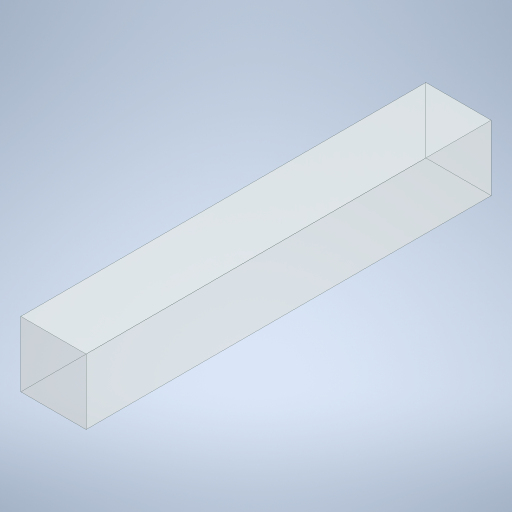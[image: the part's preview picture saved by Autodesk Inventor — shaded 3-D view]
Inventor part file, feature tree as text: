
AUTODESK INVENTOR PART (.ipt)
format: ipt  version: 2024 (Build 280153000, 153)  size: 222,720 bytes
history: native  units: in
note: dims shown in document units (in); Inventor stores cm internally (conversion verified against a paired STEP export)
features: extrude x1, sketch x1
ambient origin geometry x8: Origin, YZ Plane, XZ Plane, XY Plane, X Axis, Y Axis, Z Axis, Center Point
bodies: Solid1 (feature_tree)
feature tree (2):
  extrude  "Extrusion1"  Depth=46.5in
  sketch  "Sketch1"  dims[d2=7.5in d3=46.5in d4=7.5in d5=0.0in]
